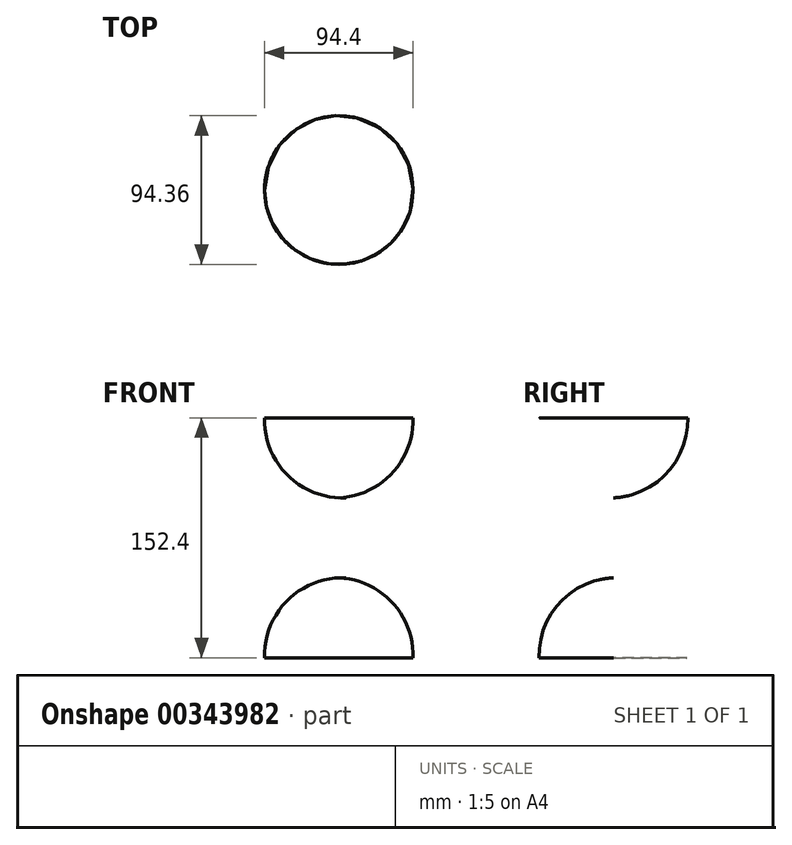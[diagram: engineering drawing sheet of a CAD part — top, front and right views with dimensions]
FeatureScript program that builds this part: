
annotation { "Feature Type Name" : "Feature", "Feature Type Description" : "" }
export const myFeature = defineFeature(function(context is Context, id is Id, definition is map)
    precondition{}
    {
        {
            var Q0;
            Q0=qCreatedBy(makeId("Front.planeOp"),FACE);
            var sketch = newSketch(context, id + "F0", { "sketchPlane" : qUnion([Q0])});
            skArc(sketch, "E0", {"start": v(-47.18, 50.8) * mm, "mid": v(-33.97, 15.76) * mm, "end": v(0, 0) * mm});
            skLineSegment(sketch, "E1", {"start": v(0, 0) * mm, "end": v(0, 49.55) * mm});
            skSolve(sketch);
        }
        {
            var Q0;
            Q0=sQuery(id+"F0.wireOp",EDGE,"E0");
            var Q1;
            Q1=sQuery(id+"F0.wireOp",EDGE,"E1");
            revolve(context, id + "F1", {"bodyType" : ToolBodyType.SURFACE, "surfaceEntities" : qUnion([Q0]), "axis" : qUnion([Q1]), "revolveType" : RevolveType.FULL});
        }
        {
            var Q0;
            Q0=qCreatedBy(makeId("Top.planeOp"),FACE);
            cPlane(context, id + "F2", {"entities" : qUnion([Q0]), "cplaneType" : CPlaneType.OFFSET, "offset" : 25.4 * mm, "oppositeDirection" : true, "width" : 152.4 * mm, "height" : 152.4 * mm});
        }
        {
            var Q0;
            Q0=makeQuery(id+"F1.opRevolve","SWEPT_BODY",BODY,{"disambiguationData":[OSD([sQuery(id+"F0.wireOp",EDGE,"E0")])]});
            var Q1;
            Q1=qCreatedBy(id+"F2.planeOp",FACE);
            mirror(context, id + "F3", {"entities" : qUnion([Q0]), "mirrorPlane" : qUnion([Q1])});
        }
    });
